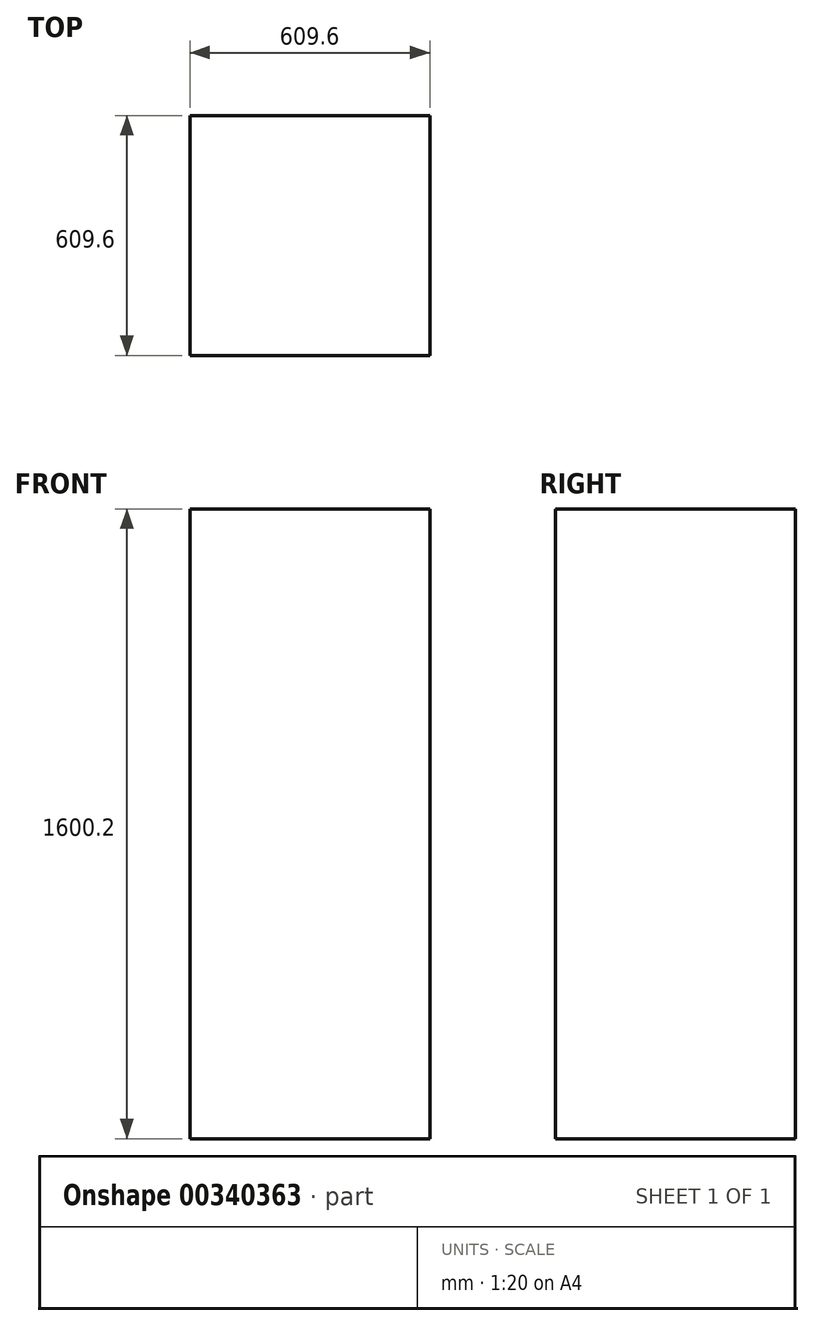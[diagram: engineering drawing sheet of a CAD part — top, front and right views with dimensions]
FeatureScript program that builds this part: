
annotation { "Feature Type Name" : "Feature", "Feature Type Description" : "" }
export const myFeature = defineFeature(function(context is Context, id is Id, definition is map)
    precondition{}
    {
        {
            var Q0;
            Q0=qCreatedBy(makeId("Front.planeOp"),FACE);
            var sketch = newSketch(context, id + "F0", { "sketchPlane" : qUnion([Q0])});
            skLineSegment(sketch, "E0.bottom", {"start": v(198.37, -756.18) * mm, "end": v(-411.23, -756.18) * mm});
            skLineSegment(sketch, "E0.top", {"start": v(198.37, 844.02) * mm, "end": v(-411.23, 844.02) * mm});
            skLineSegment(sketch, "E0.left", {"start": v(198.37, -756.18) * mm, "end": v(198.37, 844.02) * mm});
            skLineSegment(sketch, "E0.right", {"start": v(-411.23, -756.18) * mm, "end": v(-411.23, 844.02) * mm});
            skPoint(sketch, "E0.middle", {"position": v(-106.43, 43.92) * mm});
            skSolve(sketch);
        }
        {
            var Q0;
            Q0=makeQuery(id+"F0.imprint","IMPRINT",FACE,{"disambiguationData":[TD([[makeQuery(id+"F0.imprint","IMPRINT",EDGE,{"derivedFrom":sQuery(id+"F0.wireOp",EDGE,"E0.bottom")}),-1.0]])]});
            extrude(context, id + "F1", {"entities" : qUnion([Q0]), "oppositeDirection" : true, "depth" : 609.6 * mm});
        }
    });
